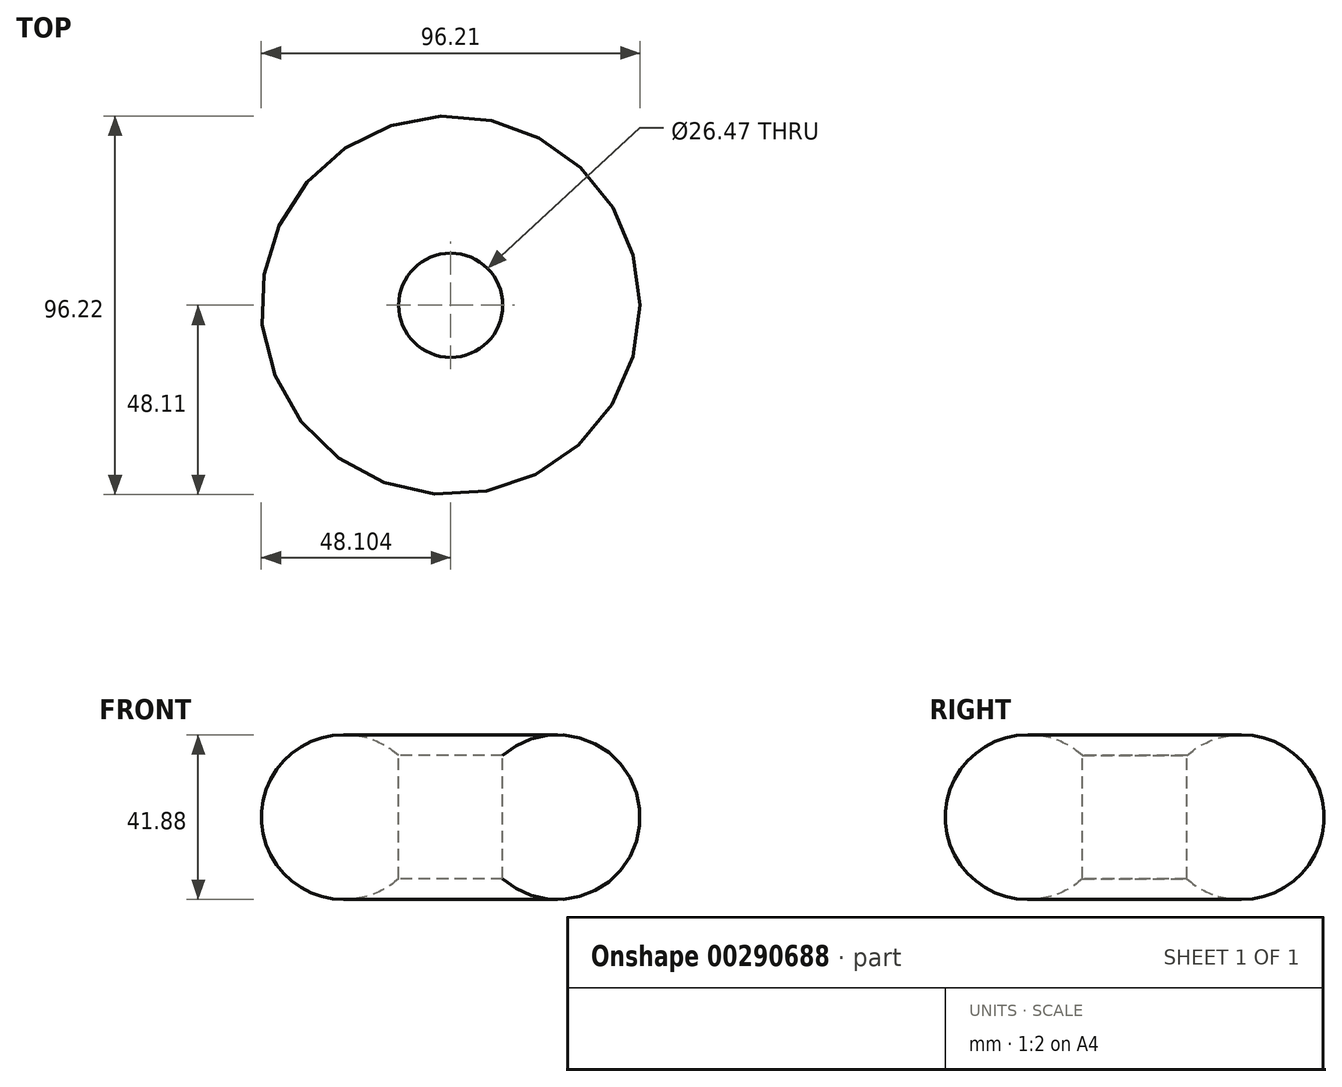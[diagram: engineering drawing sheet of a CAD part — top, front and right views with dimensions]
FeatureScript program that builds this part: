
annotation { "Feature Type Name" : "Feature", "Feature Type Description" : "" }
export const myFeature = defineFeature(function(context is Context, id is Id, definition is map)
    precondition{}
    {
        {
            var Q0;
            Q0=qCreatedBy(makeId("Front.planeOp"),FACE);
            var sketch = newSketch(context, id + "F0", { "sketchPlane" : qUnion([Q0])});
            skLineSegment(sketch, "E0", {"start": v(-36.55, 33.39) * mm, "end": v(-36.55, 4.21) * mm});
            skLineSegment(sketch, "E1", {"start": v(-23.31, 34.9) * mm, "end": v(-23.31, 3.6) * mm});
            skArc(sketch, "E2", {"start": v(-23.31, 3.6) * mm, "mid": v(11.56, 19.25) * mm, "end": v(-23.31, 34.9) * mm});
            skSolve(sketch);
        }
        {
            var Q0;
            Q0 = qSketchRegion(id + "F0", true);
            var Q1;
            Q1=sQuery(id+"F0.wireOp",EDGE,"E0");
            revolve(context, id + "F1", {"entities" : qUnion([Q0]), "axis" : qUnion([Q1]), "revolveType" : RevolveType.FULL});
        }
    });
